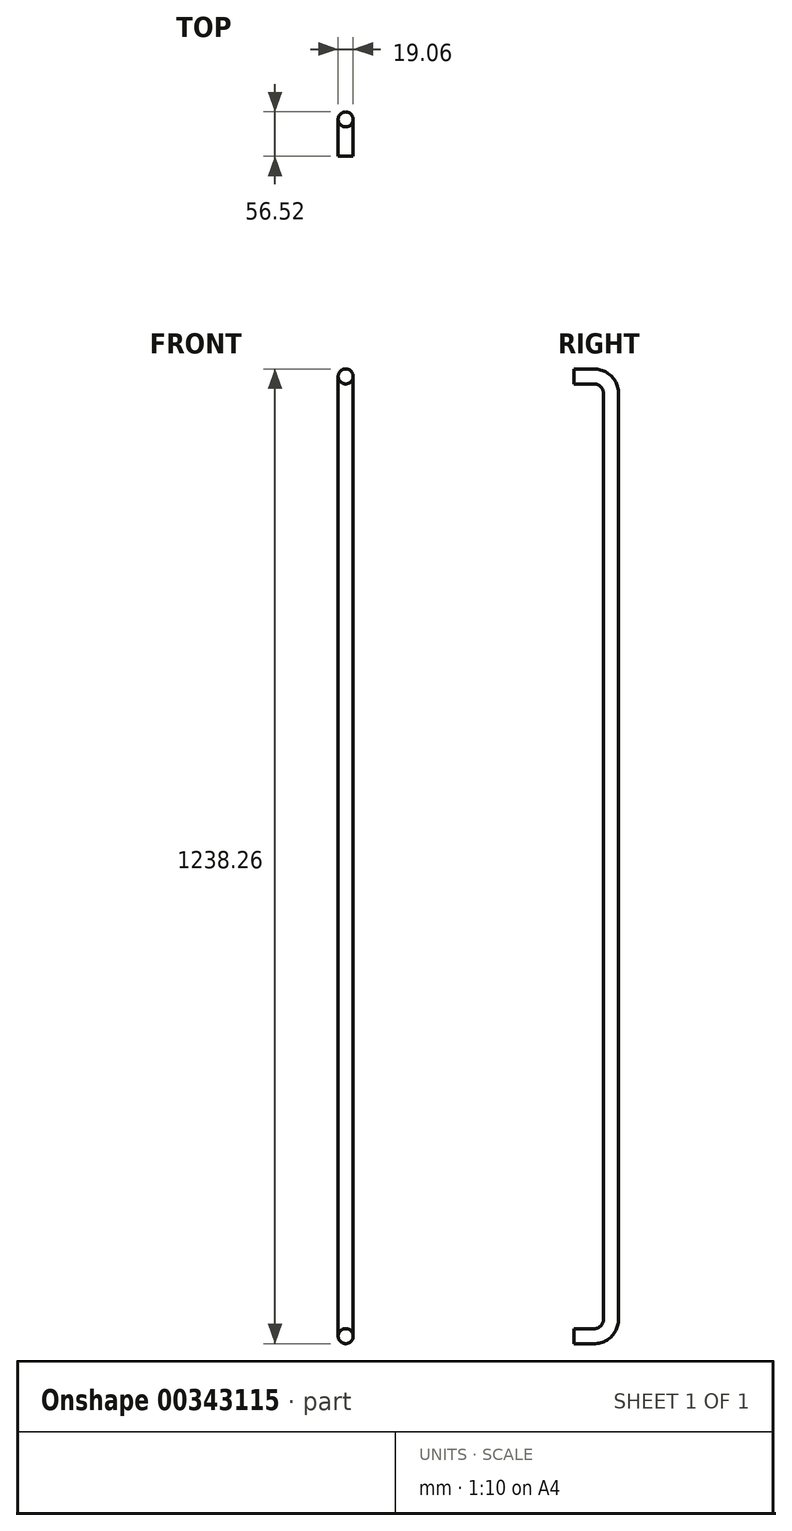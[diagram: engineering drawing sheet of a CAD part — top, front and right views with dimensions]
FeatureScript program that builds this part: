
annotation { "Feature Type Name" : "Feature", "Feature Type Description" : "" }
export const myFeature = defineFeature(function(context is Context, id is Id, definition is map)
    precondition{}
    {
        {
            var Q0;
            Q0=qCreatedBy(makeId("Right.planeOp"),FACE);
            var sketch = newSketch(context, id + "F0", { "sketchPlane" : qUnion([Q0])});
            skArc(sketch, "E0", {"start": v(0, 588) * mm, "mid": v(-6.32, 603.28) * mm, "end": v(-21.59, 609.6) * mm});
            skLineSegment(sketch, "E1", {"start": v(0, 588) * mm, "end": v(0, 0) * mm});
            skLineSegment(sketch, "E2", {"start": v(-21.59, 609.6) * mm, "end": v(-47, 609.6) * mm});
            skSolve(sketch);
        }
        {
            var Q0;
            Q0=qCreatedBy(makeId("Front.planeOp"),FACE);
            cPlane(context, id + "F1", {"entities" : qUnion([Q0]), "cplaneType" : CPlaneType.OFFSET, "offset" : 47 * mm, "width" : 152.4 * mm, "height" : 152.4 * mm});
        }
        {
            var Q0;
            Q0=qCreatedBy(id+"F1.planeOp",FACE);
            var sketch = newSketch(context, id + "F2", { "sketchPlane" : qUnion([Q0])});
            skCircle(sketch, "E3", {"center": v(0, 609.6) * mm, "radius": 9.53 * mm});
            skSolve(sketch);
        }
        {
            var Q0;
            Q0=makeQuery(id+"F2.imprint","IMPRINT",FACE,{"disambiguationData":[TD([[makeQuery(id+"F2.imprint","IMPRINT",EDGE,{"derivedFrom":sQuery(id+"F2.wireOp",EDGE,"E3")}),1.0]])]});
            var Q1;
            Q1 = qSketchRegion(id + "F0", true);
            var Q2;
            Q2 = qConstructionFilter(qBodyType(qCreatedBy(id + "F0" ,EDGE), BodyType.WIRE), ConstructionObject.NO);
            sweep(context, id + "F3", {"profiles" : qUnion([Q0, Q1]), "path" : qUnion([Q2])});
        }
        {
            var Q0;
            Q0=makeQuery(id+"F3.opSweep","SWEPT_BODY",BODY,{"disambiguationData":[OSD([sQuery(id+"F0.wireOp",EDGE,"E1"),sQuery(id+"F2.wireOp",EDGE,"E3")])]});
            var Q1;
            Q1=qCreatedBy(makeId("Top.planeOp"),FACE);
            mirror(context, id + "F4", {"operationType" : NewBodyOperationType.ADD, "entities" : qUnion([Q0]), "mirrorPlane" : qUnion([Q1])});
        }
    });
